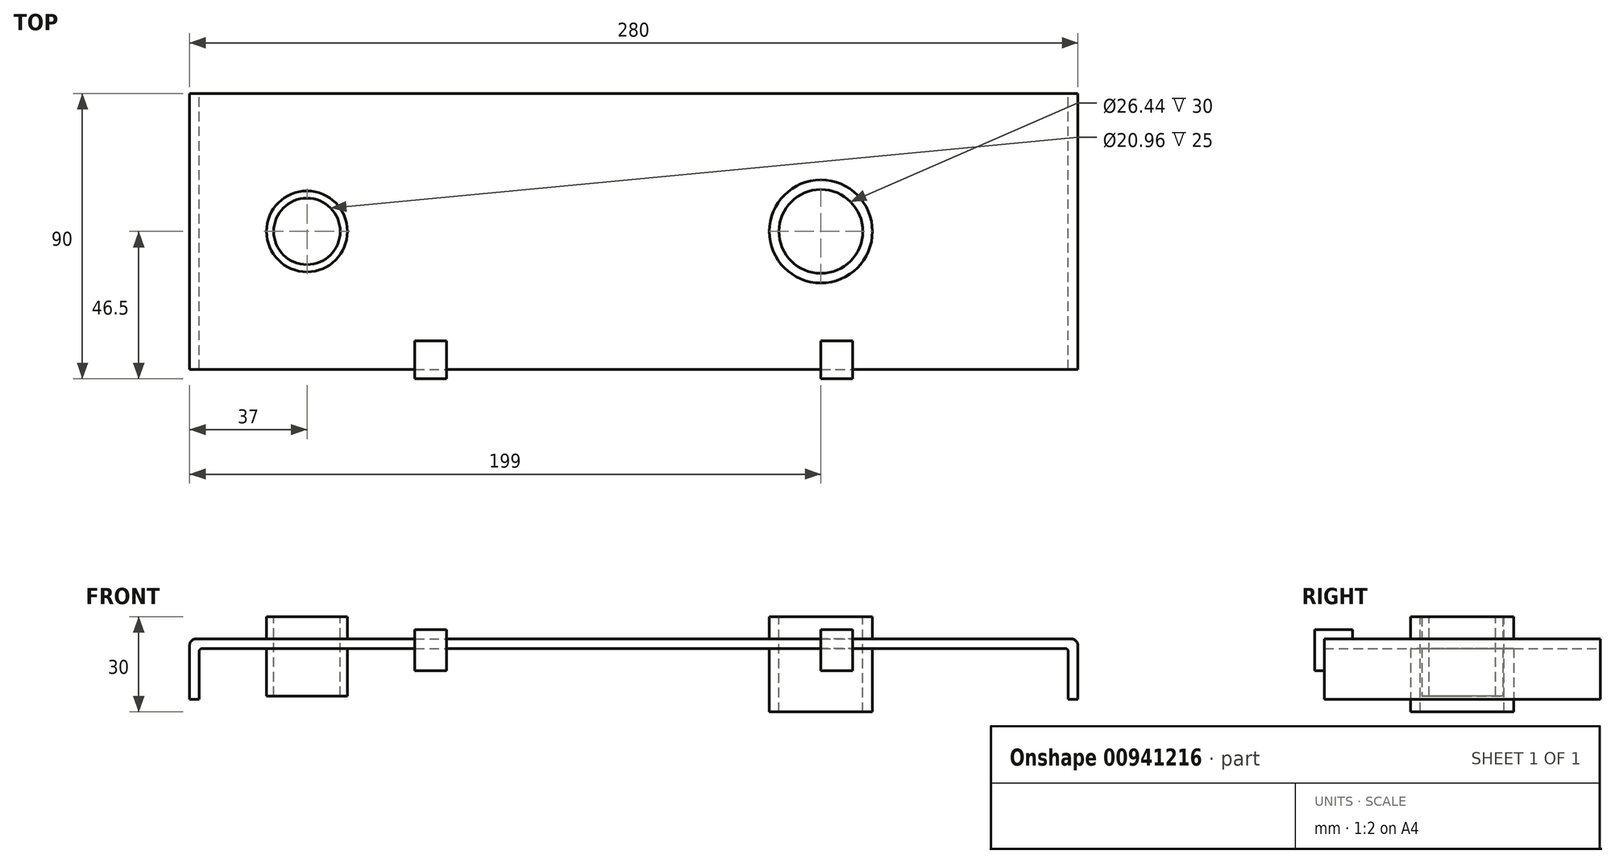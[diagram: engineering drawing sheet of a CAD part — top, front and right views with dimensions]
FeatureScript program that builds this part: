
annotation { "Feature Type Name" : "Feature", "Feature Type Description" : "" }
export const myFeature = defineFeature(function(context is Context, id is Id, definition is map)
    precondition{}
    {
        {
            var Q0;
            Q0=qCreatedBy(makeId("Front.planeOp"),FACE);
            var sketch = newSketch(context, id + "F0", { "sketchPlane" : qUnion([Q0])});
            skLineSegment(sketch, "E0", {"start": v(0, 0) * mm, "end": v(138, 0) * mm});
            skLineSegment(sketch, "E1", {"start": v(0, 0) * mm, "end": v(-138, 0) * mm});
            skLineSegment(sketch, "E2", {"start": v(-140, -2) * mm, "end": v(-140, -19) * mm});
            skLineSegment(sketch, "E3", {"start": v(140, -2) * mm, "end": v(140, -19) * mm});
            skLineSegment(sketch, "E4", {"start": v(-140, -19) * mm, "end": v(-137, -19) * mm});
            skLineSegment(sketch, "E5", {"start": v(-137, -19) * mm, "end": v(-137, -4) * mm});
            skLineSegment(sketch, "E6", {"start": v(-136, -3) * mm, "end": v(136, -3) * mm});
            skLineSegment(sketch, "E7", {"start": v(137, -4) * mm, "end": v(137, -19) * mm});
            skLineSegment(sketch, "E8", {"start": v(137, -19) * mm, "end": v(140, -19) * mm});
            skPoint(sketch, "E9.visualSharp", {"position": v(-140, 0) * mm});
            skArc(sketch, "E9.filletArc", {"start": v(-138, 0) * mm, "mid": v(-139.41, -0.59) * mm, "end": v(-140, -2) * mm});
            skPoint(sketch, "E10.visualSharp", {"position": v(140, 0) * mm});
            skArc(sketch, "E10.filletArc", {"start": v(140, -2) * mm, "mid": v(139.41, -0.59) * mm, "end": v(138, 0) * mm});
            skPoint(sketch, "E11.visualSharp", {"position": v(137, -3) * mm});
            skArc(sketch, "E11.filletArc", {"start": v(137, -4) * mm, "mid": v(136.7, -3.3) * mm, "end": v(136, -3) * mm});
            skPoint(sketch, "E12.visualSharp", {"position": v(-137, -3) * mm});
            skArc(sketch, "E12.filletArc", {"start": v(-136, -3) * mm, "mid": v(-136.7, -3.3) * mm, "end": v(-137, -4) * mm});
            skSolve(sketch);
        }
        {
            var Q0;
            Q0=makeQuery(id+"F0.imprint","IMPRINT",FACE,{"disambiguationData":[TD([[makeQuery(id+"F0.imprint","IMPRINT",EDGE,{"derivedFrom":sQuery(id+"F0.wireOp",EDGE,"E0")}),-1.0]])]});
            extrude(context, id + "F1", {"entities" : qUnion([Q0]), "depth" : 87 * mm, "offsetDistance" : 25 * mm});
        }
        {
            var Q0;
            Q0=makeQuery(id+"F1.opExtrude","SWEPT_FACE",FACE,{"disambiguationData":[OSD([sQuery(id+"F0.wireOp",EDGE,"E0"),sQuery(id+"F0.wireOp",EDGE,"E1")])]});
            var sketch = newSketch(context, id + "F2", { "sketchPlane" : qUnion([Q0])});
            skPoint(sketch, "E13", {"position": v(0, -87) * mm});
            skPoint(sketch, "E14", {"position": v(-64, -87) * mm});
            skPoint(sketch, "E15", {"position": v(64, -87) * mm});
            skLineSegment(sketch, "E16", {"start": v(-64, -87) * mm, "end": v(-69, -87) * mm});
            skLineSegment(sketch, "E17", {"start": v(-69, -87) * mm, "end": v(-69, -90) * mm});
            skLineSegment(sketch, "E18", {"start": v(-69, -90) * mm, "end": v(-59, -90) * mm});
            skLineSegment(sketch, "E19", {"start": v(-59, -90) * mm, "end": v(-59, -87) * mm});
            skLineSegment(sketch, "E20", {"start": v(-59, -87) * mm, "end": v(-64, -87) * mm});
            skLineSegment(sketch, "E21", {"start": v(64, -87) * mm, "end": v(59, -87) * mm});
            skLineSegment(sketch, "E22", {"start": v(59, -87) * mm, "end": v(59, -90) * mm});
            skLineSegment(sketch, "E23", {"start": v(59, -90) * mm, "end": v(69, -90) * mm});
            skLineSegment(sketch, "E24", {"start": v(69, -90) * mm, "end": v(69, -87) * mm});
            skLineSegment(sketch, "E25", {"start": v(69, -87) * mm, "end": v(64, -87) * mm});
            skLineSegment(sketch, "E26", {"start": v(-138, 0) * mm, "end": v(138, 0) * mm});
            skSolve(sketch);
        }
        {
            var Q0;
            Q0=qSketchRegion(id+"F2",true);
            extrude(context, id + "F3", {"entities" : qUnion([Q0]), "operationType" : NewBodyOperationType.ADD, "oppositeDirection" : true, "depth" : 10 * mm, "offsetDistance" : 25 * mm});
        }
        {
            var Q0;
            Q0=makeQuery(id+"F3.boolean.opBoolean","MERGE",FACE,{"derivedFrom":[makeQuery(id+"F1.opExtrude","SWEPT_FACE",FACE,{"disambiguationData":[OSD([sQuery(id+"F0.wireOp",EDGE,"E0"),sQuery(id+"F0.wireOp",EDGE,"E1")])]}),makeQuery(id+"F3.opExtrude","CAP_FACE",FACE,{"disambiguationData":[OSD([sQuery(id+"F2.wireOp",EDGE,"E16"),sQuery(id+"F2.wireOp",EDGE,"E17"),sQuery(id+"F2.wireOp",EDGE,"E18"),sQuery(id+"F2.wireOp",EDGE,"E19"),sQuery(id+"F2.wireOp",EDGE,"E20")])],"isStart":true}),makeQuery(id+"F3.opExtrude","CAP_FACE",FACE,{"disambiguationData":[OSD([sQuery(id+"F2.wireOp",EDGE,"E21"),sQuery(id+"F2.wireOp",EDGE,"E22"),sQuery(id+"F2.wireOp",EDGE,"E23"),sQuery(id+"F2.wireOp",EDGE,"E24"),sQuery(id+"F2.wireOp",EDGE,"E25")])],"isStart":true})]});
            var sketch = newSketch(context, id + "F4", { "sketchPlane" : qUnion([Q0])});
            skLineSegment(sketch, "E27", {"start": v(-138, 0) * mm, "end": v(-138, -87) * mm});
            skLineSegment(sketch, "E28", {"start": v(-69, -90) * mm, "end": v(-69, -78) * mm});
            skLineSegment(sketch, "E29", {"start": v(-69, -78) * mm, "end": v(-59, -78) * mm});
            skLineSegment(sketch, "E30", {"start": v(-59, -78) * mm, "end": v(-59, -90) * mm});
            skLineSegment(sketch, "E31", {"start": v(-59, -90) * mm, "end": v(-69, -90) * mm});
            skLineSegment(sketch, "E32", {"start": v(59, -90) * mm, "end": v(59, -78) * mm});
            skLineSegment(sketch, "E33", {"start": v(59, -78) * mm, "end": v(69, -78) * mm});
            skLineSegment(sketch, "E34", {"start": v(69, -78) * mm, "end": v(69, -90) * mm});
            skLineSegment(sketch, "E35", {"start": v(69, -90) * mm, "end": v(59.88, -90) * mm});
            skSolve(sketch);
        }
        {
            var Q0;
            {var subQ13=sQuery(id+"F4.wireOp",EDGE,"E29");Q0=makeQuery(id+"F4.imprint","IMPRINT",FACE,{"disambiguationData":[TD([[makeQuery(id+"F4.imprint","IMPRINT",EDGE,{"derivedFrom":subQ13}),-1.0]])]});}
            var Q1;
            {var subQ14=sQuery(id+"F4.wireOp",EDGE,"E33");Q1=makeQuery(id+"F4.imprint","IMPRINT",FACE,{"disambiguationData":[TD([[makeQuery(id+"F4.imprint","IMPRINT",EDGE,{"derivedFrom":subQ14}),-1.0]])]});}
            extrude(context, id + "F5", {"entities" : qUnion([Q0, Q1]), "operationType" : NewBodyOperationType.ADD, "depth" : 3 * mm, "offsetDistance" : 25 * mm});
        }
        {
            var Q0;
            Q0=makeQuery(id+"F3.boolean.opBoolean","MERGE",FACE,{"derivedFrom":[makeQuery(id+"F1.opExtrude","SWEPT_FACE",FACE,{"disambiguationData":[OSD([sQuery(id+"F0.wireOp",EDGE,"E0"),sQuery(id+"F0.wireOp",EDGE,"E1")])]}),makeQuery(id+"F3.opExtrude","CAP_FACE",FACE,{"disambiguationData":[OSD([sQuery(id+"F2.wireOp",EDGE,"E16"),sQuery(id+"F2.wireOp",EDGE,"E17"),sQuery(id+"F2.wireOp",EDGE,"E18"),sQuery(id+"F2.wireOp",EDGE,"E19"),sQuery(id+"F2.wireOp",EDGE,"E20")])],"isStart":true}),makeQuery(id+"F3.opExtrude","CAP_FACE",FACE,{"disambiguationData":[OSD([sQuery(id+"F2.wireOp",EDGE,"E21"),sQuery(id+"F2.wireOp",EDGE,"E22"),sQuery(id+"F2.wireOp",EDGE,"E23"),sQuery(id+"F2.wireOp",EDGE,"E24"),sQuery(id+"F2.wireOp",EDGE,"E25")])],"isStart":true})]});
            var sketch = newSketch(context, id + "F6", { "sketchPlane" : qUnion([Q0])});
            skPoint(sketch, "E36", {"position": v(59, -43.5) * mm});
            skSolve(sketch);
        }
        {
            var Q0;
            Q0=sQuery(id+"F6.wireOp",VERTEX,"E36");
            var Q1;
            Q1=makeQuery(id+"F1.opExtrude","SWEPT_BODY",BODY,{"disambiguationData":[OSD([sQuery(id+"F0.wireOp",EDGE,"E0"),sQuery(id+"F0.wireOp",EDGE,"E1"),sQuery(id+"F0.wireOp",EDGE,"E2"),sQuery(id+"F0.wireOp",EDGE,"E3"),sQuery(id+"F0.wireOp",EDGE,"E4"),sQuery(id+"F0.wireOp",EDGE,"E5"),sQuery(id+"F0.wireOp",EDGE,"E6"),sQuery(id+"F0.wireOp",EDGE,"E7"),sQuery(id+"F0.wireOp",EDGE,"E8"),sQuery(id+"F0.wireOp",EDGE,"E9.filletArc"),sQuery(id+"F0.wireOp",EDGE,"E10.filletArc"),sQuery(id+"F0.wireOp",EDGE,"E11.filletArc"),sQuery(id+"F0.wireOp",EDGE,"E12.filletArc")])]});
            hole(context, id + "F7", {"style" : HoleStyle.SIMPLE, "endStyle" : HoleEndStyle.THROUGH, "holeDiameter" : 26.44 * mm, "majorDiameter" : 5 * mm, "isTappedThrough" : true, "tappedDepth" : 5.5 * mm, "tapClearance" : 3, "locations" : qUnion([Q0]), "scope" : qUnion([Q1])});
        }
        {
            var Q0;
            Q0=makeQuery(id+"F3.boolean.opBoolean","MERGE",FACE,{"derivedFrom":[makeQuery(id+"F1.opExtrude","SWEPT_FACE",FACE,{"disambiguationData":[OSD([sQuery(id+"F0.wireOp",EDGE,"E0"),sQuery(id+"F0.wireOp",EDGE,"E1")])]}),makeQuery(id+"F3.opExtrude","CAP_FACE",FACE,{"disambiguationData":[OSD([sQuery(id+"F2.wireOp",EDGE,"E16"),sQuery(id+"F2.wireOp",EDGE,"E17"),sQuery(id+"F2.wireOp",EDGE,"E18"),sQuery(id+"F2.wireOp",EDGE,"E19"),sQuery(id+"F2.wireOp",EDGE,"E20")])],"isStart":true}),makeQuery(id+"F3.opExtrude","CAP_FACE",FACE,{"disambiguationData":[OSD([sQuery(id+"F2.wireOp",EDGE,"E21"),sQuery(id+"F2.wireOp",EDGE,"E22"),sQuery(id+"F2.wireOp",EDGE,"E23"),sQuery(id+"F2.wireOp",EDGE,"E24"),sQuery(id+"F2.wireOp",EDGE,"E25")])],"isStart":true})]});
            var sketch = newSketch(context, id + "F8", { "sketchPlane" : qUnion([Q0])});
            skPoint(sketch, "E37", {"position": v(-103, -43.5) * mm});
            skSolve(sketch);
        }
        {
            var Q0;
            Q0=sQuery(id+"F8.wireOp",VERTEX,"E37");
            var Q1;
            Q1=makeQuery(id+"F1.opExtrude","SWEPT_BODY",BODY,{"disambiguationData":[OSD([sQuery(id+"F0.wireOp",EDGE,"E0"),sQuery(id+"F0.wireOp",EDGE,"E1"),sQuery(id+"F0.wireOp",EDGE,"E2"),sQuery(id+"F0.wireOp",EDGE,"E3"),sQuery(id+"F0.wireOp",EDGE,"E4"),sQuery(id+"F0.wireOp",EDGE,"E5"),sQuery(id+"F0.wireOp",EDGE,"E6"),sQuery(id+"F0.wireOp",EDGE,"E7"),sQuery(id+"F0.wireOp",EDGE,"E8"),sQuery(id+"F0.wireOp",EDGE,"E9.filletArc"),sQuery(id+"F0.wireOp",EDGE,"E10.filletArc"),sQuery(id+"F0.wireOp",EDGE,"E11.filletArc"),sQuery(id+"F0.wireOp",EDGE,"E12.filletArc")])]});
            hole(context, id + "F9", {"style" : HoleStyle.SIMPLE, "endStyle" : HoleEndStyle.THROUGH, "holeDiameter" : 20.96 * mm, "majorDiameter" : 5 * mm, "isTappedThrough" : true, "tappedDepth" : 5.5 * mm, "tapClearance" : 3, "locations" : qUnion([Q0]), "scope" : qUnion([Q1])});
        }
        {
            var Q0;
            Q0=makeQuery(id+"F3.boolean.opBoolean","MERGE",FACE,{"derivedFrom":[makeQuery(id+"F1.opExtrude","SWEPT_FACE",FACE,{"disambiguationData":[OSD([sQuery(id+"F0.wireOp",EDGE,"E0"),sQuery(id+"F0.wireOp",EDGE,"E1")])]}),makeQuery(id+"F3.opExtrude","CAP_FACE",FACE,{"disambiguationData":[OSD([sQuery(id+"F2.wireOp",EDGE,"E16"),sQuery(id+"F2.wireOp",EDGE,"E17"),sQuery(id+"F2.wireOp",EDGE,"E18"),sQuery(id+"F2.wireOp",EDGE,"E19"),sQuery(id+"F2.wireOp",EDGE,"E20")])],"isStart":true}),makeQuery(id+"F3.opExtrude","CAP_FACE",FACE,{"disambiguationData":[OSD([sQuery(id+"F2.wireOp",EDGE,"E21"),sQuery(id+"F2.wireOp",EDGE,"E22"),sQuery(id+"F2.wireOp",EDGE,"E23"),sQuery(id+"F2.wireOp",EDGE,"E24"),sQuery(id+"F2.wireOp",EDGE,"E25")])],"isStart":true})]});
            var sketch = newSketch(context, id + "F10", { "sketchPlane" : qUnion([Q0])});
            skCircle(sketch, "E38", {"center": v(59, -43.5) * mm, "radius": 16.25 * mm});
            skCircle(sketch, "E39", {"center": v(59, -43.5) * mm, "radius": 13.22 * mm});
            skSolve(sketch);
        }
        {
            var Q0;
            Q0=makeQuery(id+"F10.imprint","IMPRINT",FACE,{"disambiguationData":[TD([[makeQuery(id+"F10.imprint","IMPRINT",EDGE,{"derivedFrom":sQuery(id+"F10.wireOp",EDGE,"E38")}),1.0]])]});
            extrude(context, id + "F11", {"entities" : qUnion([Q0]), "operationType" : NewBodyOperationType.ADD, "depth" : 7 * mm, "offsetDistance" : 25 * mm, "hasSecondDirection" : true, "secondDirectionOppositeDirection" : true, "secondDirectionDepth" : 23 * mm});
        }
        {
            var Q0;
            Q0=makeQuery(id+"F3.boolean.opBoolean","MERGE",FACE,{"derivedFrom":[makeQuery(id+"F1.opExtrude","SWEPT_FACE",FACE,{"disambiguationData":[OSD([sQuery(id+"F0.wireOp",EDGE,"E0"),sQuery(id+"F0.wireOp",EDGE,"E1")])]}),makeQuery(id+"F3.opExtrude","CAP_FACE",FACE,{"disambiguationData":[OSD([sQuery(id+"F2.wireOp",EDGE,"E16"),sQuery(id+"F2.wireOp",EDGE,"E17"),sQuery(id+"F2.wireOp",EDGE,"E18"),sQuery(id+"F2.wireOp",EDGE,"E19"),sQuery(id+"F2.wireOp",EDGE,"E20")])],"isStart":true}),makeQuery(id+"F3.opExtrude","CAP_FACE",FACE,{"disambiguationData":[OSD([sQuery(id+"F2.wireOp",EDGE,"E21"),sQuery(id+"F2.wireOp",EDGE,"E22"),sQuery(id+"F2.wireOp",EDGE,"E23"),sQuery(id+"F2.wireOp",EDGE,"E24"),sQuery(id+"F2.wireOp",EDGE,"E25")])],"isStart":true})]});
            var sketch = newSketch(context, id + "F12", { "sketchPlane" : qUnion([Q0])});
            skCircle(sketch, "E40", {"center": v(-103, -43.5) * mm, "radius": 10.48 * mm});
            skCircle(sketch, "E41", {"center": v(-103, -43.5) * mm, "radius": 12.75 * mm});
            skSolve(sketch);
        }
        {
            var Q0;
            Q0=makeQuery(id+"F12.imprint","IMPRINT",FACE,{"disambiguationData":[TD([[makeQuery(id+"F12.imprint","IMPRINT",EDGE,{"derivedFrom":sQuery(id+"F12.wireOp",EDGE,"E40")}),-1.0]])]});
            extrude(context, id + "F13", {"entities" : qUnion([Q0]), "operationType" : NewBodyOperationType.ADD, "depth" : 7 * mm, "offsetDistance" : 25 * mm, "hasSecondDirection" : true, "secondDirectionOppositeDirection" : true, "secondDirectionDepth" : 18 * mm});
        }
    });
